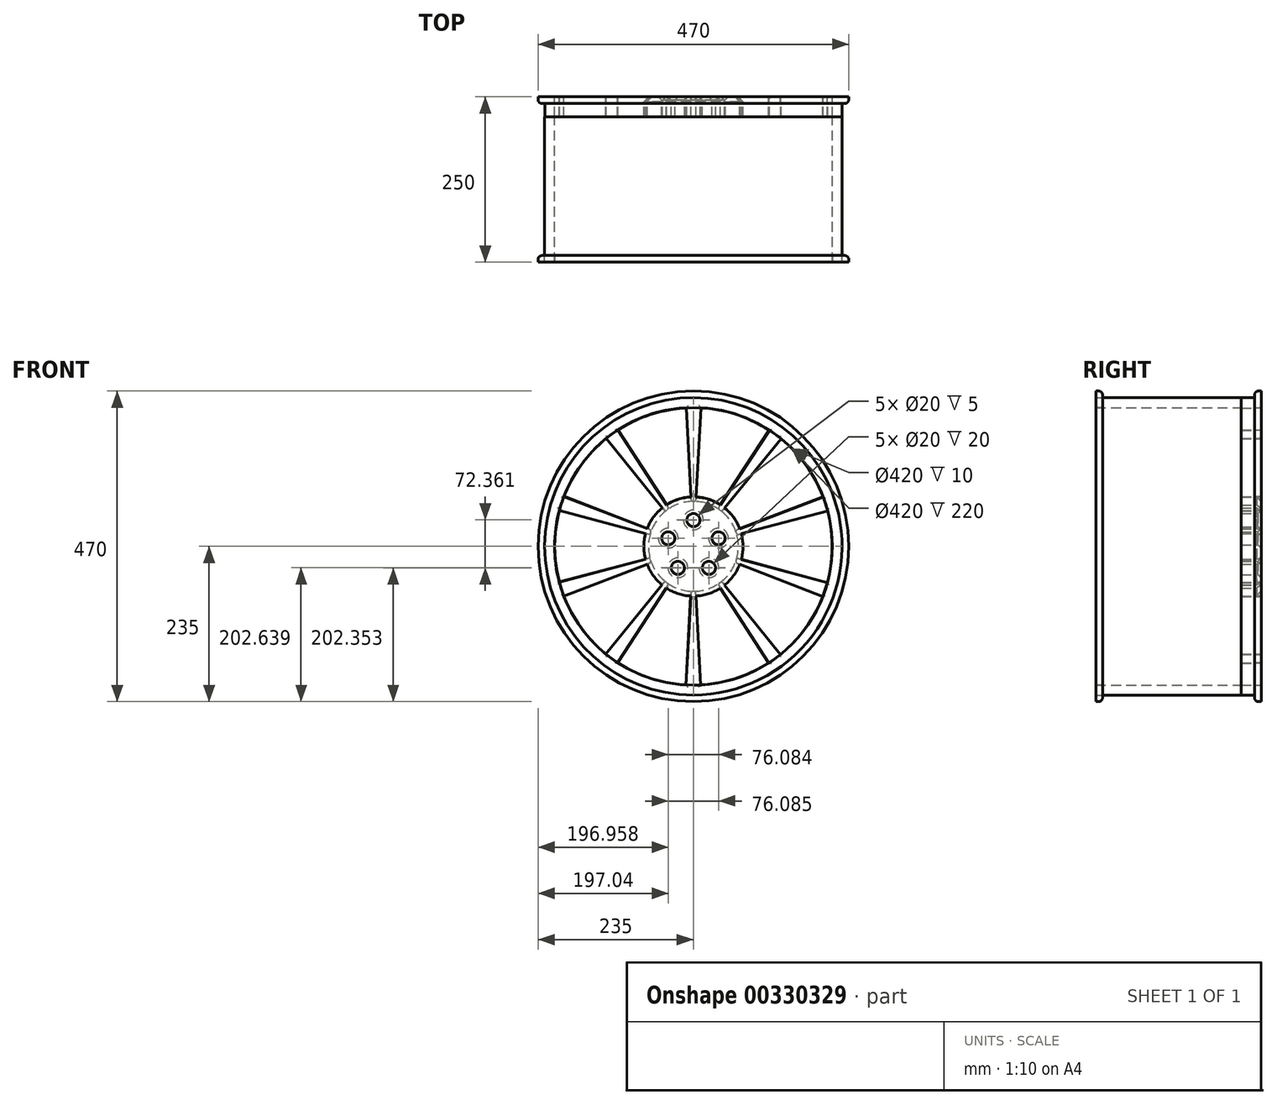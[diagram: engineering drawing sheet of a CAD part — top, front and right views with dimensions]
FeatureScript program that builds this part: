
annotation { "Feature Type Name" : "Feature", "Feature Type Description" : "" }
export const myFeature = defineFeature(function(context is Context, id is Id, definition is map)
    precondition{}
    {
        {
            var Q0;
            Q0=qCreatedBy(makeId("Front.planeOp"),FACE);
            var sketch = newSketch(context, id + "F0", { "sketchPlane" : qUnion([Q0])});
            skLineSegment(sketch, "E0", {"start": v(0, 0) * mm, "end": v(0, 225) * mm, "construction": true});
            skLineSegment(sketch, "E1.1.0", {"start": v(0, 0) * mm, "end": v(-132.25, 182.03) * mm, "construction": true});
            skLineSegment(sketch, "E1.2.0", {"start": v(0, 0) * mm, "end": v(-213.99, 69.53) * mm, "construction": true});
            skLineSegment(sketch, "E1.3.0", {"start": v(0, 0) * mm, "end": v(-213.99, -69.53) * mm, "construction": true});
            skLineSegment(sketch, "E1.4.0", {"start": v(0, 0) * mm, "end": v(-132.25, -182.03) * mm, "construction": true});
            skLineSegment(sketch, "E1.5.0", {"start": v(0, 0) * mm, "end": v(0, -225) * mm, "construction": true});
            skLineSegment(sketch, "E1.6.0", {"start": v(0, 0) * mm, "end": v(132.25, -182.03) * mm, "construction": true});
            skLineSegment(sketch, "E1.7.0", {"start": v(0, 0) * mm, "end": v(213.99, -69.53) * mm, "construction": true});
            skLineSegment(sketch, "E1.8.0", {"start": v(0, 0) * mm, "end": v(213.99, 69.53) * mm, "construction": true});
            skLineSegment(sketch, "E1.9.0", {"start": v(0, 0) * mm, "end": v(132.25, 182.03) * mm, "construction": true});
            skPoint(sketch, "E1.center", {"position": v(0, 0) * mm});
            skArc(sketch, "E2", {"start": v(-122.16, 188.95) * mm, "mid": v(-127.25, 185.56) * mm, "end": v(-132.25, 182.03) * mm, "construction": true});
            skArc(sketch, "E3", {"start": v(-141.24, 175.15) * mm, "mid": v(131.88, -182.3) * mm, "end": v(-122.16, 188.95) * mm, "construction": true});
            skArc(sketch, "E4", {"start": v(-132.25, 182.03) * mm, "mid": v(-136.79, 178.64) * mm, "end": v(-141.24, 175.15) * mm, "construction": true});
            skLineSegment(sketch, "E5", {"start": v(-69.96, 27.02) * mm, "end": v(-195.9, 75.66) * mm});
            skLineSegment(sketch, "E6", {"start": v(-72.4, 19.56) * mm, "end": v(-202.73, 54.76) * mm});
            skLineSegment(sketch, "E7", {"start": v(-72.48, -19.26) * mm, "end": v(-202.95, -53.94) * mm});
            skLineSegment(sketch, "E8", {"start": v(-70.07, -26.74) * mm, "end": v(-70.07, -26.74) * mm});
            skLineSegment(sketch, "E9", {"start": v(-40.98, -62.82) * mm, "end": v(-114.73, -175.89) * mm});
            skLineSegment(sketch, "E10", {"start": v(-47.32, -58.19) * mm, "end": v(-132.49, -162.93) * mm});
            skLineSegment(sketch, "E11", {"start": v(-4.08, -74.89) * mm, "end": v(-11.42, -209.69) * mm});
            skLineSegment(sketch, "E12", {"start": v(3.77, -74.9) * mm, "end": v(10.56, -209.73) * mm});
            skLineSegment(sketch, "E13", {"start": v(40.72, -62.98) * mm, "end": v(114.02, -176.35) * mm});
            skLineSegment(sketch, "E14", {"start": v(47.08, -58.38) * mm, "end": v(131.82, -163.47) * mm});
            skLineSegment(sketch, "E15", {"start": v(69.96, -27.02) * mm, "end": v(195.9, -75.66) * mm});
            skLineSegment(sketch, "E16", {"start": v(72.4, -19.56) * mm, "end": v(202.73, -54.76) * mm});
            skLineSegment(sketch, "E17", {"start": v(70.07, 26.74) * mm, "end": v(196.2, 74.86) * mm});
            skLineSegment(sketch, "E18", {"start": v(72.48, 19.26) * mm, "end": v(202.95, 53.94) * mm});
            skLineSegment(sketch, "E19", {"start": v(47.32, 58.19) * mm, "end": v(132.49, 162.93) * mm});
            skLineSegment(sketch, "E20", {"start": v(40.98, 62.82) * mm, "end": v(114.73, 175.89) * mm});
            skLineSegment(sketch, "E21", {"start": v(4.08, 74.89) * mm, "end": v(11.42, 209.69) * mm});
            skLineSegment(sketch, "E22", {"start": v(-3.77, 74.9) * mm, "end": v(-10.56, 209.73) * mm});
            skLineSegment(sketch, "E23", {"start": v(-40.72, 62.98) * mm, "end": v(-114.02, 176.35) * mm});
            skLineSegment(sketch, "E24", {"start": v(-47.08, 58.38) * mm, "end": v(-131.82, 163.47) * mm});
            skCircle(sketch, "E25", {"center": v(0, 0) * mm, "radius": 40 * mm, "construction": true});
            skCircle(sketch, "E26", {"center": v(0, 40) * mm, "radius": 10 * mm});
            skCircle(sketch, "E27.1.0", {"center": v(-38.04, 12.36) * mm, "radius": 10 * mm});
            skCircle(sketch, "E27.2.0", {"center": v(-23.51, -32.36) * mm, "radius": 10 * mm});
            skCircle(sketch, "E27.3.0", {"center": v(23.51, -32.36) * mm, "radius": 10 * mm});
            skCircle(sketch, "E27.4.0", {"center": v(38.04, 12.36) * mm, "radius": 10 * mm});
            skCircle(sketch, "E28", {"center": v(0, 0) * mm, "radius": 235 * mm});
            skLineSegment(sketch, "E29", {"start": v(-131.82, 163.47) * mm, "end": v(-131.82, 163.47) * mm});
            skArc(sketch, "E30", {"start": v(-131.82, 163.47) * mm, "mid": v(-169.64, 123.78) * mm, "end": v(-195.9, 75.66) * mm});
            skArc(sketch, "E31", {"start": v(-10.56, 209.73) * mm, "mid": v(-64.49, 199.85) * mm, "end": v(-114.02, 176.35) * mm});
            skArc(sketch, "E32", {"start": v(114.73, 175.89) * mm, "mid": v(65.3, 199.59) * mm, "end": v(11.42, 209.69) * mm});
            skArc(sketch, "E33", {"start": v(196.2, 74.86) * mm, "mid": v(170.14, 123.09) * mm, "end": v(132.49, 162.93) * mm});
            skLineSegment(sketch, "E34", {"start": v(202.95, 53.94) * mm, "end": v(202.95, 53.94) * mm});
            skArc(sketch, "E35", {"start": v(202.73, -54.76) * mm, "mid": v(210, -0.43) * mm, "end": v(202.95, 53.94) * mm});
            skArc(sketch, "E36", {"start": v(131.82, -163.47) * mm, "mid": v(169.64, -123.78) * mm, "end": v(195.9, -75.66) * mm});
            skArc(sketch, "E37", {"start": v(10.56, -209.73) * mm, "mid": v(64.49, -199.85) * mm, "end": v(114.02, -176.35) * mm});
            skArc(sketch, "E38", {"start": v(-114.73, -175.89) * mm, "mid": v(-65.3, -199.59) * mm, "end": v(-11.42, -209.69) * mm});
            skLineSegment(sketch, "E39", {"start": v(196.2, 74.86) * mm, "end": v(196.2, 74.86) * mm});
            skArc(sketch, "E40", {"start": v(-202.73, 54.76) * mm, "mid": v(-210, 0.43) * mm, "end": v(-202.95, -53.94) * mm});
            skLineSegment(sketch, "E41", {"start": v(-195.9, 75.66) * mm, "end": v(-195.9, 75.66) * mm});
            skArc(sketch, "E42", {"start": v(-196.2, -74.86) * mm, "mid": v(-170.14, -123.09) * mm, "end": v(-132.49, -162.93) * mm});
            skArc(sketch, "E43", {"start": v(-202.95, -53.94) * mm, "mid": v(-199.85, -64.49) * mm, "end": v(-196.2, -74.86) * mm});
            skArc(sketch, "E44", {"start": v(-40.98, -62.82) * mm, "mid": v(-23.32, -71.28) * mm, "end": v(-4.08, -74.89) * mm});
            skLineSegment(sketch, "E45", {"start": v(-72.48, -19.26) * mm, "end": v(-72.48, -19.26) * mm});
            skLineSegment(sketch, "E46", {"start": v(-70.07, -26.74) * mm, "end": v(-196.2, -74.86) * mm});
            skArc(sketch, "E47", {"start": v(-70.07, -26.74) * mm, "mid": v(-60.77, -43.96) * mm, "end": v(-47.32, -58.19) * mm});
            skArc(sketch, "E48", {"start": v(3.77, -74.9) * mm, "mid": v(23.03, -71.38) * mm, "end": v(40.72, -62.98) * mm});
            skArc(sketch, "E49", {"start": v(47.08, -58.38) * mm, "mid": v(60.59, -44.2) * mm, "end": v(69.96, -27.02) * mm});
            skArc(sketch, "E50", {"start": v(72.4, -19.56) * mm, "mid": v(75, -0.15) * mm, "end": v(72.48, 19.26) * mm});
            skArc(sketch, "E51", {"start": v(70.07, 26.74) * mm, "mid": v(60.77, 43.96) * mm, "end": v(47.32, 58.19) * mm});
            skArc(sketch, "E52", {"start": v(40.98, 62.82) * mm, "mid": v(23.32, 71.28) * mm, "end": v(4.08, 74.89) * mm});
            skArc(sketch, "E53", {"start": v(-3.77, 74.9) * mm, "mid": v(-23.03, 71.38) * mm, "end": v(-40.72, 62.98) * mm});
            skArc(sketch, "E54", {"start": v(-47.08, 58.38) * mm, "mid": v(-60.59, 44.2) * mm, "end": v(-69.96, 27.02) * mm});
            skArc(sketch, "E55", {"start": v(-72.4, 19.56) * mm, "mid": v(-75, 0.15) * mm, "end": v(-72.48, -19.26) * mm});
            skSolve(sketch);
        }
        {
            var Q0;
            Q0 = qSketchRegion(id + "F0", true);
            extrude(context, id + "F1", {"entities" : qUnion([Q0]), "depth" : 10 * mm});
        }
        {
            var Q0;
            Q0=makeQuery(id+"F1.opExtrude","CAP_FACE",FACE,{"disambiguationData":[OSD([sQuery(id+"F0.wireOp",EDGE,"E5"),sQuery(id+"F0.wireOp",EDGE,"E6"),sQuery(id+"F0.wireOp",EDGE,"E7"),sQuery(id+"F0.wireOp",EDGE,"E9"),sQuery(id+"F0.wireOp",EDGE,"E10"),sQuery(id+"F0.wireOp",EDGE,"E11"),sQuery(id+"F0.wireOp",EDGE,"E12"),sQuery(id+"F0.wireOp",EDGE,"E13"),sQuery(id+"F0.wireOp",EDGE,"E14"),sQuery(id+"F0.wireOp",EDGE,"E15"),sQuery(id+"F0.wireOp",EDGE,"E16"),sQuery(id+"F0.wireOp",EDGE,"E17"),sQuery(id+"F0.wireOp",EDGE,"E18"),sQuery(id+"F0.wireOp",EDGE,"E19"),sQuery(id+"F0.wireOp",EDGE,"E20"),sQuery(id+"F0.wireOp",EDGE,"E21"),sQuery(id+"F0.wireOp",EDGE,"E22"),sQuery(id+"F0.wireOp",EDGE,"E23"),sQuery(id+"F0.wireOp",EDGE,"E24"),sQuery(id+"F0.wireOp",EDGE,"E26"),sQuery(id+"F0.wireOp",EDGE,"E27.1.0"),sQuery(id+"F0.wireOp",EDGE,"E27.2.0"),sQuery(id+"F0.wireOp",EDGE,"E27.3.0"),sQuery(id+"F0.wireOp",EDGE,"E27.4.0"),sQuery(id+"F0.wireOp",EDGE,"E28"),sQuery(id+"F0.wireOp",EDGE,"E30"),sQuery(id+"F0.wireOp",EDGE,"E31"),sQuery(id+"F0.wireOp",EDGE,"E32"),sQuery(id+"F0.wireOp",EDGE,"E33"),sQuery(id+"F0.wireOp",EDGE,"E35"),sQuery(id+"F0.wireOp",EDGE,"E36"),sQuery(id+"F0.wireOp",EDGE,"E37"),sQuery(id+"F0.wireOp",EDGE,"E38"),sQuery(id+"F0.wireOp",EDGE,"E40"),sQuery(id+"F0.wireOp",EDGE,"E42"),sQuery(id+"F0.wireOp",EDGE,"E44"),sQuery(id+"F0.wireOp",EDGE,"E46"),sQuery(id+"F0.wireOp",EDGE,"E47"),sQuery(id+"F0.wireOp",EDGE,"E48"),sQuery(id+"F0.wireOp",EDGE,"E49"),sQuery(id+"F0.wireOp",EDGE,"E50"),sQuery(id+"F0.wireOp",EDGE,"E51"),sQuery(id+"F0.wireOp",EDGE,"E52"),sQuery(id+"F0.wireOp",EDGE,"E53"),sQuery(id+"F0.wireOp",EDGE,"E54"),sQuery(id+"F0.wireOp",EDGE,"E55")])],"isStart":false});
            var sketch = newSketch(context, id + "F2", { "sketchPlane" : qUnion([Q0])});
            skLineSegment(sketch, "E56", {"start": v(0.08, -0.29) * mm, "end": v(0.08, 224.71) * mm, "construction": true});
            skLineSegment(sketch, "E57.1.0", {"start": v(0.08, -0.29) * mm, "end": v(-132.17, 181.74) * mm, "construction": true});
            skLineSegment(sketch, "E57.2.0", {"start": v(0.08, -0.29) * mm, "end": v(-213.9, 69.24) * mm, "construction": true});
            skLineSegment(sketch, "E57.3.0", {"start": v(0.08, -0.29) * mm, "end": v(-213.9, -69.82) * mm, "construction": true});
            skLineSegment(sketch, "E57.4.0", {"start": v(0.08, -0.29) * mm, "end": v(-132.17, -182.32) * mm, "construction": true});
            skLineSegment(sketch, "E57.5.0", {"start": v(0.08, -0.29) * mm, "end": v(0.08, -225.29) * mm, "construction": true});
            skLineSegment(sketch, "E57.6.0", {"start": v(0.08, -0.29) * mm, "end": v(132.33, -182.32) * mm, "construction": true});
            skLineSegment(sketch, "E57.7.0", {"start": v(0.08, -0.29) * mm, "end": v(214.07, -69.82) * mm, "construction": true});
            skLineSegment(sketch, "E57.8.0", {"start": v(0.08, -0.29) * mm, "end": v(214.07, 69.24) * mm, "construction": true});
            skLineSegment(sketch, "E57.9.0", {"start": v(0.08, -0.29) * mm, "end": v(132.33, 181.74) * mm, "construction": true});
            skPoint(sketch, "E57.center", {"position": v(0.08, -0.29) * mm});
            skArc(sketch, "E58", {"start": v(-122.08, 188.66) * mm, "mid": v(-127.17, 185.27) * mm, "end": v(-132.17, 181.74) * mm, "construction": true});
            skArc(sketch, "E59", {"start": v(-141.16, 174.86) * mm, "mid": v(131.96, -182.58) * mm, "end": v(-122.08, 188.66) * mm});
            skArc(sketch, "E60", {"start": v(-132.17, 181.74) * mm, "mid": v(-136.7, 178.36) * mm, "end": v(-141.16, 174.86) * mm, "construction": true});
            skLineSegment(sketch, "E61", {"start": v(-69.88, 26.73) * mm, "end": v(-195.82, 75.37) * mm});
            skLineSegment(sketch, "E62", {"start": v(-72.32, 19.27) * mm, "end": v(-202.65, 54.48) * mm});
            skLineSegment(sketch, "E63", {"start": v(-72.4, -19.55) * mm, "end": v(-202.87, -54.23) * mm});
            skLineSegment(sketch, "E64", {"start": v(-40.9, -63.1) * mm, "end": v(-114.65, -176.17) * mm});
            skLineSegment(sketch, "E65", {"start": v(-47.24, -58.48) * mm, "end": v(-132.4, -163.22) * mm});
            skLineSegment(sketch, "E66", {"start": v(-4, -75.18) * mm, "end": v(-11.34, -209.98) * mm});
            skLineSegment(sketch, "E67", {"start": v(3.85, -75.2) * mm, "end": v(10.65, -210.02) * mm});
            skLineSegment(sketch, "E68", {"start": v(40.8, -63.27) * mm, "end": v(114.1, -176.64) * mm});
            skLineSegment(sketch, "E69", {"start": v(47.16, -58.67) * mm, "end": v(131.9, -163.76) * mm});
            skLineSegment(sketch, "E70", {"start": v(70.05, -27.3) * mm, "end": v(195.98, -75.94) * mm});
            skLineSegment(sketch, "E71", {"start": v(72.49, -19.85) * mm, "end": v(202.82, -55.05) * mm});
            skLineSegment(sketch, "E72", {"start": v(70.16, 26.45) * mm, "end": v(196.29, 74.57) * mm});
            skLineSegment(sketch, "E73", {"start": v(72.57, 18.98) * mm, "end": v(203.04, 53.65) * mm});
            skLineSegment(sketch, "E74", {"start": v(47.4, 57.9) * mm, "end": v(132.57, 162.65) * mm});
            skLineSegment(sketch, "E75", {"start": v(41.06, 62.53) * mm, "end": v(114.81, 175.6) * mm});
            skLineSegment(sketch, "E76", {"start": v(4.16, 74.6) * mm, "end": v(11.5, 209.4) * mm});
            skLineSegment(sketch, "E77", {"start": v(-3.7, 74.62) * mm, "end": v(-10.48, 209.45) * mm});
            skLineSegment(sketch, "E78", {"start": v(-40.64, 62.7) * mm, "end": v(-113.93, 176.07) * mm});
            skLineSegment(sketch, "E79", {"start": v(-47, 58.1) * mm, "end": v(-131.74, 163.18) * mm});
            skCircle(sketch, "E80", {"center": v(0.08, -0.29) * mm, "radius": 40 * mm, "construction": true});
            skCircle(sketch, "E81", {"center": v(0.08, 39.71) * mm, "radius": 10 * mm});
            skCircle(sketch, "E82.1.0", {"center": v(-37.96, 12.07) * mm, "radius": 10 * mm});
            skCircle(sketch, "E82.2.0", {"center": v(-23.43, -32.65) * mm, "radius": 10 * mm});
            skCircle(sketch, "E82.3.0", {"center": v(23.6, -32.65) * mm, "radius": 10 * mm});
            skCircle(sketch, "E82.4.0", {"center": v(38.12, 12.07) * mm, "radius": 10 * mm});
            skCircle(sketch, "E83", {"center": v(0.08, -0.29) * mm, "radius": 235 * mm, "construction": true});
            skArc(sketch, "E84", {"start": v(-131.74, 163.18) * mm, "mid": v(-169.56, 123.5) * mm, "end": v(-195.82, 75.37) * mm});
            skArc(sketch, "E85", {"start": v(-10.48, 209.45) * mm, "mid": v(-64.4, 199.57) * mm, "end": v(-113.93, 176.07) * mm});
            skArc(sketch, "E86", {"start": v(114.81, 175.6) * mm, "mid": v(65.38, 199.3) * mm, "end": v(11.5, 209.4) * mm});
            skArc(sketch, "E87", {"start": v(196.29, 74.57) * mm, "mid": v(170.23, 122.8) * mm, "end": v(132.57, 162.65) * mm});
            skArc(sketch, "E88", {"start": v(202.82, -55.05) * mm, "mid": v(210.08, -0.71) * mm, "end": v(203.04, 53.65) * mm});
            skArc(sketch, "E89", {"start": v(131.9, -163.76) * mm, "mid": v(169.72, -124.07) * mm, "end": v(195.98, -75.94) * mm});
            skArc(sketch, "E90", {"start": v(10.65, -210.02) * mm, "mid": v(64.57, -200.14) * mm, "end": v(114.1, -176.64) * mm});
            skArc(sketch, "E91", {"start": v(-114.65, -176.17) * mm, "mid": v(-65.22, -199.88) * mm, "end": v(-11.34, -209.98) * mm});
            skArc(sketch, "E92", {"start": v(-202.65, 54.48) * mm, "mid": v(-209.92, 0.14) * mm, "end": v(-202.87, -54.23) * mm});
            skArc(sketch, "E93", {"start": v(-196.12, -75.14) * mm, "mid": v(-170.06, -123.38) * mm, "end": v(-132.4, -163.22) * mm});
            skArc(sketch, "E94", {"start": v(-202.87, -54.23) * mm, "mid": v(-199.77, -64.77) * mm, "end": v(-196.12, -75.14) * mm});
            skArc(sketch, "E95", {"start": v(-40.9, -63.1) * mm, "mid": v(-23.24, -71.57) * mm, "end": v(-4, -75.18) * mm});
            skLineSegment(sketch, "E96", {"start": v(213.3, -96.22) * mm, "end": v(213.3, -96.22) * mm});
            skLineSegment(sketch, "E97", {"start": v(210.9, -88.75) * mm, "end": v(210.9, -88.75) * mm});
            skLineSegment(sketch, "E98", {"start": v(-70, -27.02) * mm, "end": v(-196.12, -75.14) * mm});
            skArc(sketch, "E99", {"start": v(-70, -27.02) * mm, "mid": v(-60.68, -44.25) * mm, "end": v(-47.24, -58.48) * mm});
            skArc(sketch, "E100", {"start": v(3.85, -75.2) * mm, "mid": v(23.11, -71.66) * mm, "end": v(40.8, -63.27) * mm});
            skArc(sketch, "E101", {"start": v(47.16, -58.67) * mm, "mid": v(60.67, -44.5) * mm, "end": v(70.05, -27.3) * mm});
            skArc(sketch, "E102", {"start": v(72.49, -19.85) * mm, "mid": v(75.08, -0.44) * mm, "end": v(72.57, 18.98) * mm});
            skArc(sketch, "E103", {"start": v(70.16, 26.45) * mm, "mid": v(60.85, 43.67) * mm, "end": v(47.4, 57.9) * mm});
            skArc(sketch, "E104", {"start": v(41.06, 62.53) * mm, "mid": v(23.4, 71) * mm, "end": v(4.16, 74.6) * mm});
            skArc(sketch, "E105", {"start": v(-3.7, 74.62) * mm, "mid": v(-22.95, 71.1) * mm, "end": v(-40.64, 62.7) * mm});
            skArc(sketch, "E106", {"start": v(-47, 58.1) * mm, "mid": v(-60.5, 43.92) * mm, "end": v(-69.88, 26.73) * mm});
            skArc(sketch, "E107", {"start": v(-72.32, 19.27) * mm, "mid": v(-74.92, -0.13) * mm, "end": v(-72.4, -19.55) * mm});
            skArc(sketch, "E108", {"start": v(-122.08, 188.66) * mm, "mid": v(-131.8, 182.01) * mm, "end": v(-141.16, 174.86) * mm});
            skSolve(sketch);
        }
        {
            var Q0;
            Q0 = qSketchRegion(id + "F2", true);
            extrude(context, id + "F3", {"entities" : qUnion([Q0]), "operationType" : NewBodyOperationType.ADD, "depth" : 20 * mm});
        }
        {
            var Q0;
            Q0=makeQuery(id+"F3.opExtrude","CAP_FACE",FACE,{"disambiguationData":[OSD([sQuery(id+"F2.wireOp",EDGE,"E59"),sQuery(id+"F2.wireOp",EDGE,"E61"),sQuery(id+"F2.wireOp",EDGE,"E62"),sQuery(id+"F2.wireOp",EDGE,"E63"),sQuery(id+"F2.wireOp",EDGE,"E64"),sQuery(id+"F2.wireOp",EDGE,"E65"),sQuery(id+"F2.wireOp",EDGE,"E66"),sQuery(id+"F2.wireOp",EDGE,"E67"),sQuery(id+"F2.wireOp",EDGE,"E68"),sQuery(id+"F2.wireOp",EDGE,"E69"),sQuery(id+"F2.wireOp",EDGE,"E70"),sQuery(id+"F2.wireOp",EDGE,"E71"),sQuery(id+"F2.wireOp",EDGE,"E72"),sQuery(id+"F2.wireOp",EDGE,"E73"),sQuery(id+"F2.wireOp",EDGE,"E74"),sQuery(id+"F2.wireOp",EDGE,"E75"),sQuery(id+"F2.wireOp",EDGE,"E76"),sQuery(id+"F2.wireOp",EDGE,"E77"),sQuery(id+"F2.wireOp",EDGE,"E78"),sQuery(id+"F2.wireOp",EDGE,"E79"),sQuery(id+"F2.wireOp",EDGE,"E81"),sQuery(id+"F2.wireOp",EDGE,"E82.1.0"),sQuery(id+"F2.wireOp",EDGE,"E82.2.0"),sQuery(id+"F2.wireOp",EDGE,"E82.3.0"),sQuery(id+"F2.wireOp",EDGE,"E82.4.0"),sQuery(id+"F2.wireOp",EDGE,"E84"),sQuery(id+"F2.wireOp",EDGE,"E85"),sQuery(id+"F2.wireOp",EDGE,"E86"),sQuery(id+"F2.wireOp",EDGE,"E87"),sQuery(id+"F2.wireOp",EDGE,"E88"),sQuery(id+"F2.wireOp",EDGE,"E89"),sQuery(id+"F2.wireOp",EDGE,"E90"),sQuery(id+"F2.wireOp",EDGE,"E91"),sQuery(id+"F2.wireOp",EDGE,"E92"),sQuery(id+"F2.wireOp",EDGE,"E93"),sQuery(id+"F2.wireOp",EDGE,"E95"),sQuery(id+"F2.wireOp",EDGE,"E98"),sQuery(id+"F2.wireOp",EDGE,"E99"),sQuery(id+"F2.wireOp",EDGE,"E100"),sQuery(id+"F2.wireOp",EDGE,"E101"),sQuery(id+"F2.wireOp",EDGE,"E102"),sQuery(id+"F2.wireOp",EDGE,"E103"),sQuery(id+"F2.wireOp",EDGE,"E104"),sQuery(id+"F2.wireOp",EDGE,"E105"),sQuery(id+"F2.wireOp",EDGE,"E106"),sQuery(id+"F2.wireOp",EDGE,"E107"),sQuery(id+"F2.wireOp",EDGE,"E108")])],"isStart":false});
            var sketch = newSketch(context, id + "F4", { "sketchPlane" : qUnion([Q0])});
            skCircle(sketch, "E109", {"center": v(0, 0) * mm, "radius": 210 * mm});
            skCircle(sketch, "E110", {"center": v(0, 0) * mm, "radius": 225 * mm});
            skSolve(sketch);
        }
        {
            var Q0;
            Q0 = qSketchRegion(id + "F4", true);
            extrude(context, id + "F5", {"entities" : qUnion([Q0]), "operationType" : NewBodyOperationType.ADD, "depth" : 220 * mm});
        }
        {
            var Q0;
            Q0=makeQuery(id+"F5.opExtrude","CAP_FACE",FACE,{"disambiguationData":[OSD([sQuery(id+"F4.wireOp",EDGE,"E109"),sQuery(id+"F4.wireOp",EDGE,"E110")])],"isStart":false});
            var sketch = newSketch(context, id + "F6", { "sketchPlane" : qUnion([Q0])});
            skCircle(sketch, "E111", {"center": v(0, 0) * mm, "radius": 210 * mm});
            skCircle(sketch, "E112", {"center": v(0, 0) * mm, "radius": 235 * mm});
            skSolve(sketch);
        }
        {
            var Q0;
            Q0 = qSketchRegion(id + "F6", true);
            extrude(context, id + "F7", {"entities" : qUnion([Q0]), "oppositeDirection" : true, "depth" : 10 * mm});
        }
        {
            var Q0;
            Q0=makeQuery(id+"F1.opExtrude","CAP_EDGE",EDGE,{"disambiguationData":[OSD([sQuery(id+"F0.wireOp",EDGE,"E27.4.0")])],"isStart":true});
            var Q1;
            Q1=makeQuery(id+"F1.opExtrude","CAP_EDGE",EDGE,{"disambiguationData":[OSD([sQuery(id+"F0.wireOp",EDGE,"E26")])],"isStart":true});
            var Q2;
            Q2=makeQuery(id+"F1.opExtrude","CAP_EDGE",EDGE,{"disambiguationData":[OSD([sQuery(id+"F0.wireOp",EDGE,"E27.1.0")])],"isStart":true});
            var Q3;
            Q3=makeQuery(id+"F1.opExtrude","CAP_EDGE",EDGE,{"disambiguationData":[OSD([sQuery(id+"F0.wireOp",EDGE,"E27.2.0")])],"isStart":true});
            var Q4;
            Q4=makeQuery(id+"F1.opExtrude","CAP_EDGE",EDGE,{"disambiguationData":[OSD([sQuery(id+"F0.wireOp",EDGE,"E27.3.0")])],"isStart":true});
            chamfer(context, id + "F8", {"entities" : qUnion([Q0, Q1, Q2, Q3, Q4]), "width" : 5 * mm, "tangentPropagation" : true});
        }
        {
            var Q0;
            Q0=makeQuery(id+"F1.opExtrude","CAP_EDGE",EDGE,{"disambiguationData":[OSD([sQuery(id+"F0.wireOp",EDGE,"E28")])],"isStart":false});
            fillet(context, id + "F9", {"entities" : qUnion([Q0]), "radius" : 6 * mm, "tangentPropagation" : true, "allowEdgeOverflow" : false});
        }
        {
            var Q0;
            Q0=makeQuery(id+"F7.opExtrude","CAP_EDGE",EDGE,{"disambiguationData":[OSD([sQuery(id+"F6.wireOp",EDGE,"E112")])],"isStart":false});
            fillet(context, id + "F10", {"entities" : qUnion([Q0]), "radius" : 6 * mm, "tangentPropagation" : true, "allowEdgeOverflow" : false});
        }
        {
            var Q0;
            Q0=makeQuery(id+"F1.opExtrude","CAP_EDGE",EDGE,{"disambiguationData":[OSD([sQuery(id+"F0.wireOp",EDGE,"E52")])],"isStart":true});
            var Q1;
            Q1=makeQuery(id+"F1.opExtrude","CAP_EDGE",EDGE,{"disambiguationData":[OSD([sQuery(id+"F0.wireOp",EDGE,"E53")])],"isStart":true});
            var Q2;
            Q2=makeQuery(id+"F1.opExtrude","CAP_EDGE",EDGE,{"disambiguationData":[OSD([sQuery(id+"F0.wireOp",EDGE,"E54")])],"isStart":true});
            var Q3;
            Q3=makeQuery(id+"F1.opExtrude","CAP_EDGE",EDGE,{"disambiguationData":[OSD([sQuery(id+"F0.wireOp",EDGE,"E55")])],"isStart":true});
            var Q4;
            Q4=makeQuery(id+"F1.opExtrude","CAP_EDGE",EDGE,{"disambiguationData":[OSD([sQuery(id+"F0.wireOp",EDGE,"E47")])],"isStart":true});
            var Q5;
            Q5=makeQuery(id+"F1.opExtrude","CAP_EDGE",EDGE,{"disambiguationData":[OSD([sQuery(id+"F0.wireOp",EDGE,"E44")])],"isStart":true});
            var Q6;
            Q6=makeQuery(id+"F1.opExtrude","CAP_EDGE",EDGE,{"disambiguationData":[OSD([sQuery(id+"F0.wireOp",EDGE,"E48")])],"isStart":true});
            var Q7;
            Q7=makeQuery(id+"F1.opExtrude","CAP_EDGE",EDGE,{"disambiguationData":[OSD([sQuery(id+"F0.wireOp",EDGE,"E49")])],"isStart":true});
            var Q8;
            Q8=makeQuery(id+"F1.opExtrude","CAP_EDGE",EDGE,{"disambiguationData":[OSD([sQuery(id+"F0.wireOp",EDGE,"E50")])],"isStart":true});
            var Q9;
            Q9=makeQuery(id+"F1.opExtrude","CAP_EDGE",EDGE,{"disambiguationData":[OSD([sQuery(id+"F0.wireOp",EDGE,"E51")])],"isStart":true});
            chamfer(context, id + "F11", {"entities" : qUnion([Q0, Q1, Q2, Q3, Q4, Q5, Q6, Q7, Q8, Q9]), "width" : 7 * mm, "tangentPropagation" : true});
        }
        {
            var Q0;
            Q0=makeQuery(id+"F1.opExtrude","CAP_EDGE",EDGE,{"disambiguationData":[OSD([sQuery(id+"F0.wireOp",EDGE,"E33")])],"isStart":true});
            var Q1;
            Q1=makeQuery(id+"F1.opExtrude","CAP_EDGE",EDGE,{"disambiguationData":[OSD([sQuery(id+"F0.wireOp",EDGE,"E19")])],"isStart":true});
            var Q2;
            Q2=makeQuery(id+"F1.opExtrude","CAP_EDGE",EDGE,{"disambiguationData":[OSD([sQuery(id+"F0.wireOp",EDGE,"E21")])],"isStart":true});
            var Q3;
            Q3=makeQuery(id+"F1.opExtrude","CAP_EDGE",EDGE,{"disambiguationData":[OSD([sQuery(id+"F0.wireOp",EDGE,"E31")])],"isStart":true});
            var Q4;
            Q4=makeQuery(id+"F1.opExtrude","CAP_EDGE",EDGE,{"disambiguationData":[OSD([sQuery(id+"F0.wireOp",EDGE,"E32")])],"isStart":true});
            var Q5;
            Q5=makeQuery(id+"F1.opExtrude","CAP_EDGE",EDGE,{"disambiguationData":[OSD([sQuery(id+"F0.wireOp",EDGE,"E30")])],"isStart":true});
            var Q6;
            Q6=makeQuery(id+"F1.opExtrude","CAP_EDGE",EDGE,{"disambiguationData":[OSD([sQuery(id+"F0.wireOp",EDGE,"E40")])],"isStart":true});
            var Q7;
            Q7=makeQuery(id+"F1.opExtrude","CAP_EDGE",EDGE,{"disambiguationData":[OSD([sQuery(id+"F0.wireOp",EDGE,"E42")])],"isStart":true});
            var Q8;
            Q8=makeQuery(id+"F1.opExtrude","CAP_EDGE",EDGE,{"disambiguationData":[OSD([sQuery(id+"F0.wireOp",EDGE,"E38")])],"isStart":true});
            var Q9;
            Q9=makeQuery(id+"F1.opExtrude","CAP_EDGE",EDGE,{"disambiguationData":[OSD([sQuery(id+"F0.wireOp",EDGE,"E35")])],"isStart":true});
            var Q10;
            Q10=makeQuery(id+"F1.opExtrude","CAP_EDGE",EDGE,{"disambiguationData":[OSD([sQuery(id+"F0.wireOp",EDGE,"E36")])],"isStart":true});
            var Q11;
            Q11=makeQuery(id+"F1.opExtrude","CAP_EDGE",EDGE,{"disambiguationData":[OSD([sQuery(id+"F0.wireOp",EDGE,"E37")])],"isStart":true});
            var Q12;
            Q12=makeQuery(id+"F1.opExtrude","CAP_EDGE",EDGE,{"disambiguationData":[OSD([sQuery(id+"F0.wireOp",EDGE,"E22")])],"isStart":true});
            var Q13;
            Q13=makeQuery(id+"F1.opExtrude","CAP_EDGE",EDGE,{"disambiguationData":[OSD([sQuery(id+"F0.wireOp",EDGE,"E23")])],"isStart":true});
            var Q14;
            Q14=makeQuery(id+"F1.opExtrude","CAP_EDGE",EDGE,{"disambiguationData":[OSD([sQuery(id+"F0.wireOp",EDGE,"E24")])],"isStart":true});
            var Q15;
            Q15=makeQuery(id+"F1.opExtrude","CAP_EDGE",EDGE,{"disambiguationData":[OSD([sQuery(id+"F0.wireOp",EDGE,"E20")])],"isStart":true});
            var Q16;
            Q16=makeQuery(id+"F1.opExtrude","CAP_EDGE",EDGE,{"disambiguationData":[OSD([sQuery(id+"F0.wireOp",EDGE,"E18")])],"isStart":true});
            var Q17;
            Q17=makeQuery(id+"F1.opExtrude","CAP_EDGE",EDGE,{"disambiguationData":[OSD([sQuery(id+"F0.wireOp",EDGE,"E17")])],"isStart":true});
            var Q18;
            Q18=makeQuery(id+"F1.opExtrude","CAP_EDGE",EDGE,{"disambiguationData":[OSD([sQuery(id+"F0.wireOp",EDGE,"E15")])],"isStart":true});
            var Q19;
            Q19=makeQuery(id+"F1.opExtrude","CAP_EDGE",EDGE,{"disambiguationData":[OSD([sQuery(id+"F0.wireOp",EDGE,"E13")])],"isStart":true});
            var Q20;
            Q20=makeQuery(id+"F1.opExtrude","CAP_EDGE",EDGE,{"disambiguationData":[OSD([sQuery(id+"F0.wireOp",EDGE,"E11")])],"isStart":true});
            var Q21;
            Q21=makeQuery(id+"F1.opExtrude","CAP_EDGE",EDGE,{"disambiguationData":[OSD([sQuery(id+"F0.wireOp",EDGE,"E10")])],"isStart":true});
            var Q22;
            Q22=makeQuery(id+"F1.opExtrude","CAP_EDGE",EDGE,{"disambiguationData":[OSD([sQuery(id+"F0.wireOp",EDGE,"E46")])],"isStart":true});
            var Q23;
            Q23=makeQuery(id+"F1.opExtrude","CAP_EDGE",EDGE,{"disambiguationData":[OSD([sQuery(id+"F0.wireOp",EDGE,"E6")])],"isStart":true});
            var Q24;
            Q24=makeQuery(id+"F1.opExtrude","CAP_EDGE",EDGE,{"disambiguationData":[OSD([sQuery(id+"F0.wireOp",EDGE,"E7")])],"isStart":true});
            var Q25;
            Q25=makeQuery(id+"F1.opExtrude","CAP_EDGE",EDGE,{"disambiguationData":[OSD([sQuery(id+"F0.wireOp",EDGE,"E9")])],"isStart":true});
            var Q26;
            Q26=makeQuery(id+"F1.opExtrude","CAP_EDGE",EDGE,{"disambiguationData":[OSD([sQuery(id+"F0.wireOp",EDGE,"E12")])],"isStart":true});
            var Q27;
            Q27=makeQuery(id+"F1.opExtrude","CAP_EDGE",EDGE,{"disambiguationData":[OSD([sQuery(id+"F0.wireOp",EDGE,"E14")])],"isStart":true});
            var Q28;
            Q28=makeQuery(id+"F1.opExtrude","CAP_EDGE",EDGE,{"disambiguationData":[OSD([sQuery(id+"F0.wireOp",EDGE,"E16")])],"isStart":true});
            var Q29;
            Q29=makeQuery(id+"F1.opExtrude","CAP_EDGE",EDGE,{"disambiguationData":[OSD([sQuery(id+"F0.wireOp",EDGE,"E5")])],"isStart":true});
            fillet(context, id + "F12", {"entities" : qUnion([Q0, Q1, Q2, Q3, Q4, Q5, Q6, Q7, Q8, Q9, Q10, Q11, Q12, Q13, Q14, Q15, Q16, Q17, Q18, Q19, Q20, Q21, Q22, Q23, Q24, Q25, Q26, Q27, Q28, Q29]), "radius" : 3 * mm, "tangentPropagation" : true, "allowEdgeOverflow" : false});
        }
    });
